# Revit family: IS_Dea_T3486_BIM_GB
name_source: partatom
category: Plumbing Fixtures
revit_build: Autodesk Revit MEP 2014 (Build: 20140709_2115(x64)
units: mm (PartAtom-declared; Revit-internal decimal feet)

## types (2) — shared parameters
Accessories = www.idealspec.co.uk
AreaUnits = millimeters
Assembly Code = C1030200
AssetType = Fixed
BIMObjectName = ISI_IdealStandard_WCPans_Dea_T348601
BREEAMApproved = No
Brand = Ideal Standard
CodePerformance = Vitreous china to BS 3402
ConnectionType = Plumbing
Description = Dea wall mounted wc pan with horizontal outlet with aquablade technology
DurationUnit = year
ECA = No
ExpectedLife = 30
Features = Wall mounted wc pan with horizontal outlet with aquablade technology
Finish = White
IfcExportAs = IfcSanitaryTerminalType
IfcExportType = TOILETPAN
InstallationInstructions = www.idealspec.co.uk/resources.html
LinearUnits = millimeters
ManufacturerURL = www.idealspec.co.uk
NBSDescription = WC pans
NBSReference = 45-30-70/384
NettWeight = 23.5 Kg
NominalHeight = 354 mm
NominalLength = 551 mm
NominalWidth = 366 mm
PanColor = White
PanMaterial = Vitreous china
PanMounting = BackToWall
Shape = Sculptured
Size = 366 x 551 x 354 mm
Space = Internal
SpilloverLevel = 400 mm
ToiletPanType = WashDown
ToiletType = Other
URL = www.idealspec.co.uk
Uniclass2015Description = WC pans
Uniclass2015Reference = Pr_40_20_93_94
Uniclass2015Version = Products v1.1
Version = 1
VolumeUnits = Litres
WRAS = No
WarrantyDescription = Manufacturers Warranty
WarrantyDurationParts = 99
WarrantyDurationUnit = year
WaterEfficientProduct = No
zero-valued in all types: CWFU, Cost, Default Elevation, HWFU, NominalDepth, WFU

## per-type parameters (varying)
| type | BarCode | Model | ModelNumber | Name | ProductInformation |
| T348683-Dea Wh Bowl Matt White | 8014140429227 | T348683 | T348683 | ISI_WCPans_Dea_T348683_IdealStandard | www.idealspec.co.uk/assets/datasheet/T348683 |
| T348601-Dea Wh Bowl White | 8014140429173 | T348601 | T348601 | ISI_WCPans_Dea_T348601_IdealStandard | www.idealspec.co.uk/assets/datasheet/T348601 |

## geometry (parser evidence)
native form markers: Sweep x3
no freeform markers — native parametric forms only
